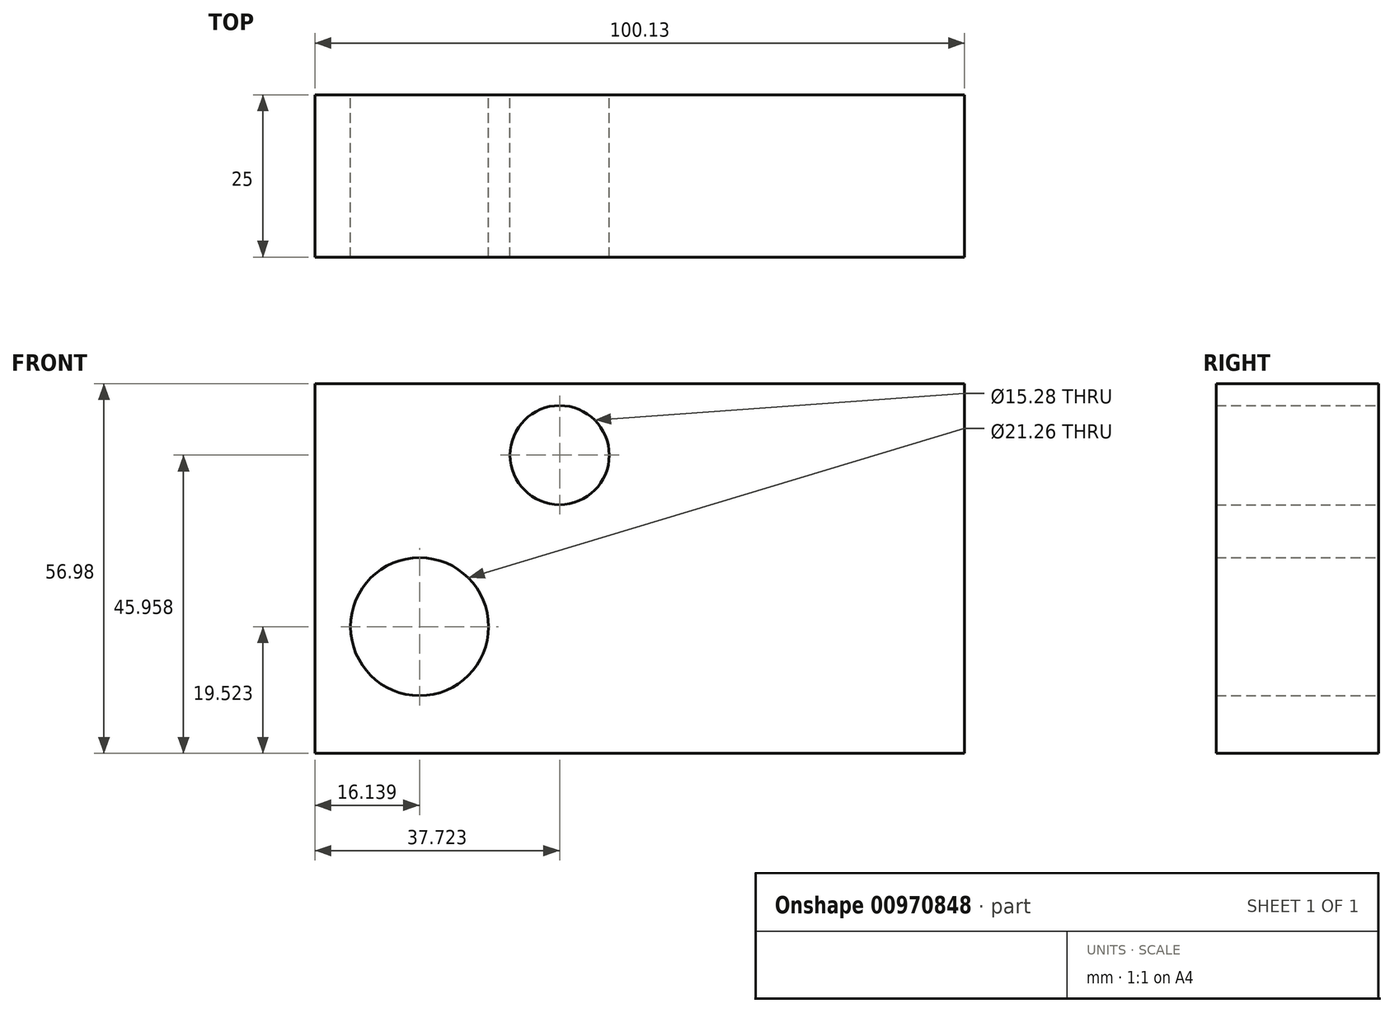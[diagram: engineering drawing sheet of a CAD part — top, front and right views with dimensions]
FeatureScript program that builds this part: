
annotation { "Feature Type Name" : "Feature", "Feature Type Description" : "" }
export const myFeature = defineFeature(function(context is Context, id is Id, definition is map)
    precondition{}
    {
        {
            var Q0;
            Q0=qCreatedBy(makeId("Front.planeOp"),FACE);
            var sketch = newSketch(context, id + "F0", { "sketchPlane" : qUnion([Q0])});
            skLineSegment(sketch, "E0.bottom", {"start": v(-59.1, 34.52) * mm, "end": v(41.03, 34.52) * mm});
            skLineSegment(sketch, "E0.top", {"start": v(-59.1, -22.46) * mm, "end": v(41.03, -22.46) * mm});
            skLineSegment(sketch, "E0.left", {"start": v(-59.1, 34.52) * mm, "end": v(-59.1, -22.46) * mm});
            skLineSegment(sketch, "E0.right", {"start": v(41.03, 34.52) * mm, "end": v(41.03, -22.46) * mm});
            skSolve(sketch);
        }
        {
            var Q0;
            Q0=makeQuery(id+"F0.imprint","IMPRINT",FACE,{"disambiguationData":[TD([[makeQuery(id+"F0.imprint","IMPRINT",EDGE,{"derivedFrom":sQuery(id+"F0.wireOp",EDGE,"E0.bottom")}),-1.0]])]});
            extrude(context, id + "F1", {"entities" : qUnion([Q0]), "depth" : 25 * mm, "offsetDistance" : 25 * mm});
        }
        {
            var Q0;
            Q0=qCreatedBy(makeId("Front.planeOp"),FACE);
            var sketch = newSketch(context, id + "F2", { "sketchPlane" : qUnion([Q0])});
            skCircle(sketch, "E1", {"center": v(-21.38, 23.5) * mm, "radius": 7.64 * mm});
            skSolve(sketch);
        }
        {
            var Q0;
            Q0 = qSketchRegion(id + "F2", true);
            extrude(context, id + "F3", {"entities" : qUnion([Q0]), "operationType" : NewBodyOperationType.REMOVE, "depth" : 120.5 * mm, "offsetDistance" : 25 * mm});
        }
        {
            var Q0;
            Q0=qCreatedBy(makeId("Front.planeOp"),FACE);
            var sketch = newSketch(context, id + "F4", { "sketchPlane" : qUnion([Q0])});
            skCircle(sketch, "E2", {"center": v(-42.96, -2.94) * mm, "radius": 10.63 * mm});
            skSolve(sketch);
        }
        {
            var Q0;
            Q0 = qSketchRegion(id + "F4", true);
            extrude(context, id + "F5", {"entities" : qUnion([Q0]), "operationType" : NewBodyOperationType.REMOVE, "depth" : 179 * mm, "offsetDistance" : 25 * mm});
        }
    });
